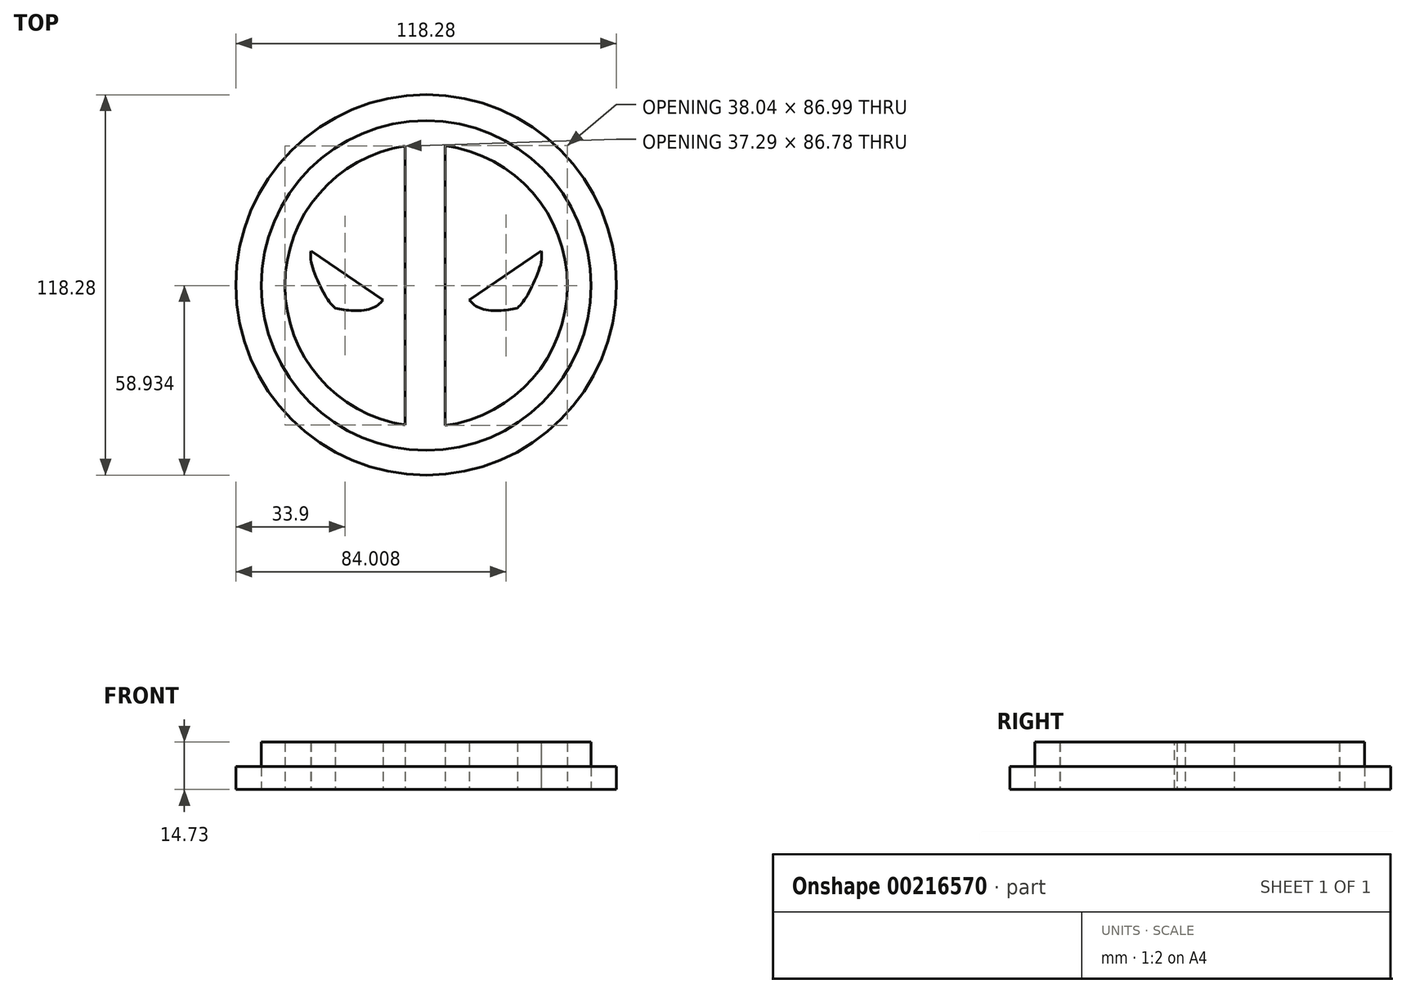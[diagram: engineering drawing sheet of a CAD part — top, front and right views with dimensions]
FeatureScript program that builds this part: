
annotation { "Feature Type Name" : "Feature", "Feature Type Description" : "" }
export const myFeature = defineFeature(function(context is Context, id is Id, definition is map)
    precondition{}
    {
        {
            var Q0;
            Q0=qCreatedBy(makeId("Top.planeOp"),FACE);
            var sketch = newSketch(context, id + "F0", { "sketchPlane" : qUnion([Q0])});
            skCircle(sketch, "E0", {"center": v(0, -3.84) * mm, "radius": 51.25 * mm});
            skArc(sketch, "E1.0", {"start": v(5.85, -47.33) * mm, "mid": v(43.89, -3.84) * mm, "end": v(5.85, 39.66) * mm});
            skLineSegment(sketch, "E2", {"start": v(-6.6, 39.55) * mm, "end": v(-6.6, -47.23) * mm});
            skLineSegment(sketch, "E3", {"start": v(5.85, 39.66) * mm, "end": v(5.85, -47.33) * mm});
            skLineSegment(sketch, "E4", {"start": v(-35.79, 6.91) * mm, "end": v(-13.4, -8.36) * mm});
            skFitSpline(sketch, "E5", {"points": [v(-13.4, -8.36) * mm, v(-15.2, -10.05) * mm, v(-18.82, -11.41) * mm, v(-24.02, -11.52) * mm, v(-28.32, -10.85) * mm], "startDerivative": vector(-8.01, -9) * mm, "endDerivative": vector(-15.7, 3.03) * mm});
            skFitSpline(sketch, "E6", {"points": [v(-35.79, 6.91) * mm, v(-35.79, 3.74) * mm, v(-33.53, -2.7) * mm, v(-30.47, -8.36) * mm, v(-28.32, -10.85) * mm], "startDerivative": vector(-1.49, -14.24) * mm, "endDerivative": vector(10.28, -10.53) * mm});
            skLineSegment(sketch, "E7.MirrorCS", {"start": v(35.79, 6.91) * mm, "end": v(13.4, -8.36) * mm});
            skFitSpline(sketch, "E8.MirrorCS", {"points": [v(13.4, -8.36) * mm, v(15.2, -10.05) * mm, v(18.82, -11.41) * mm, v(24.02, -11.52) * mm, v(28.32, -10.85) * mm], "startDerivative": vector(8.01, -9) * mm, "endDerivative": vector(15.7, 3.03) * mm});
            skFitSpline(sketch, "E9.MirrorCS", {"points": [v(35.79, 6.91) * mm, v(35.79, 3.74) * mm, v(33.53, -2.7) * mm, v(30.47, -8.36) * mm, v(28.32, -10.85) * mm], "startDerivative": vector(1.49, -14.24) * mm, "endDerivative": vector(-10.28, -10.53) * mm});
            skArc(sketch, "E10.trimOffspring", {"start": v(-6.6, 39.55) * mm, "mid": v(-43.89, -3.84) * mm, "end": v(-6.6, -47.23) * mm});
            skSolve(sketch);
        }
        {
            var Q0;
            Q0=qCreatedBy(makeId("Top.planeOp"),FACE);
            var sketch = newSketch(context, id + "F1", { "sketchPlane" : qUnion([Q0])});
            skCircle(sketch, "E11", {"center": v(0, -3.63) * mm, "radius": 59.14 * mm});
            skSolve(sketch);
        }
        {
            var Q0;
            Q0 = qSketchRegion(id + "F0", true);
            var Q1;
            Q1=makeQuery(id+"F0.imprint","IMPRINT",FACE,{"disambiguationData":[TD([[makeQuery(id+"F0.imprint","IMPRINT",EDGE,{"derivedFrom":sQuery(id+"F0.wireOp",EDGE,"E4")}),-1.0]])]});
            var Q2;
            Q2=makeQuery(id+"F0.imprint","IMPRINT",FACE,{"disambiguationData":[TD([[makeQuery(id+"F0.imprint","IMPRINT",EDGE,{"derivedFrom":sQuery(id+"F0.wireOp",EDGE,"E8.MirrorCS")}),1.0]])]});
            extrude(context, id + "F2", {"entities" : qUnion([Q0, Q1, Q2]), "depth" : 14.73 * mm});
        }
        {
            var Q0;
            Q0=makeQuery(id+"F1.imprint","IMPRINT",FACE,{"disambiguationData":[TD([[makeQuery(id+"F1.imprint","IMPRINT",EDGE,{"derivedFrom":sQuery(id+"F1.wireOp",EDGE,"E11")}),1.0]])]});
            extrude(context, id + "F3", {"entities" : qUnion([Q0]), "depth" : 7.11 * mm});
        }
    });
